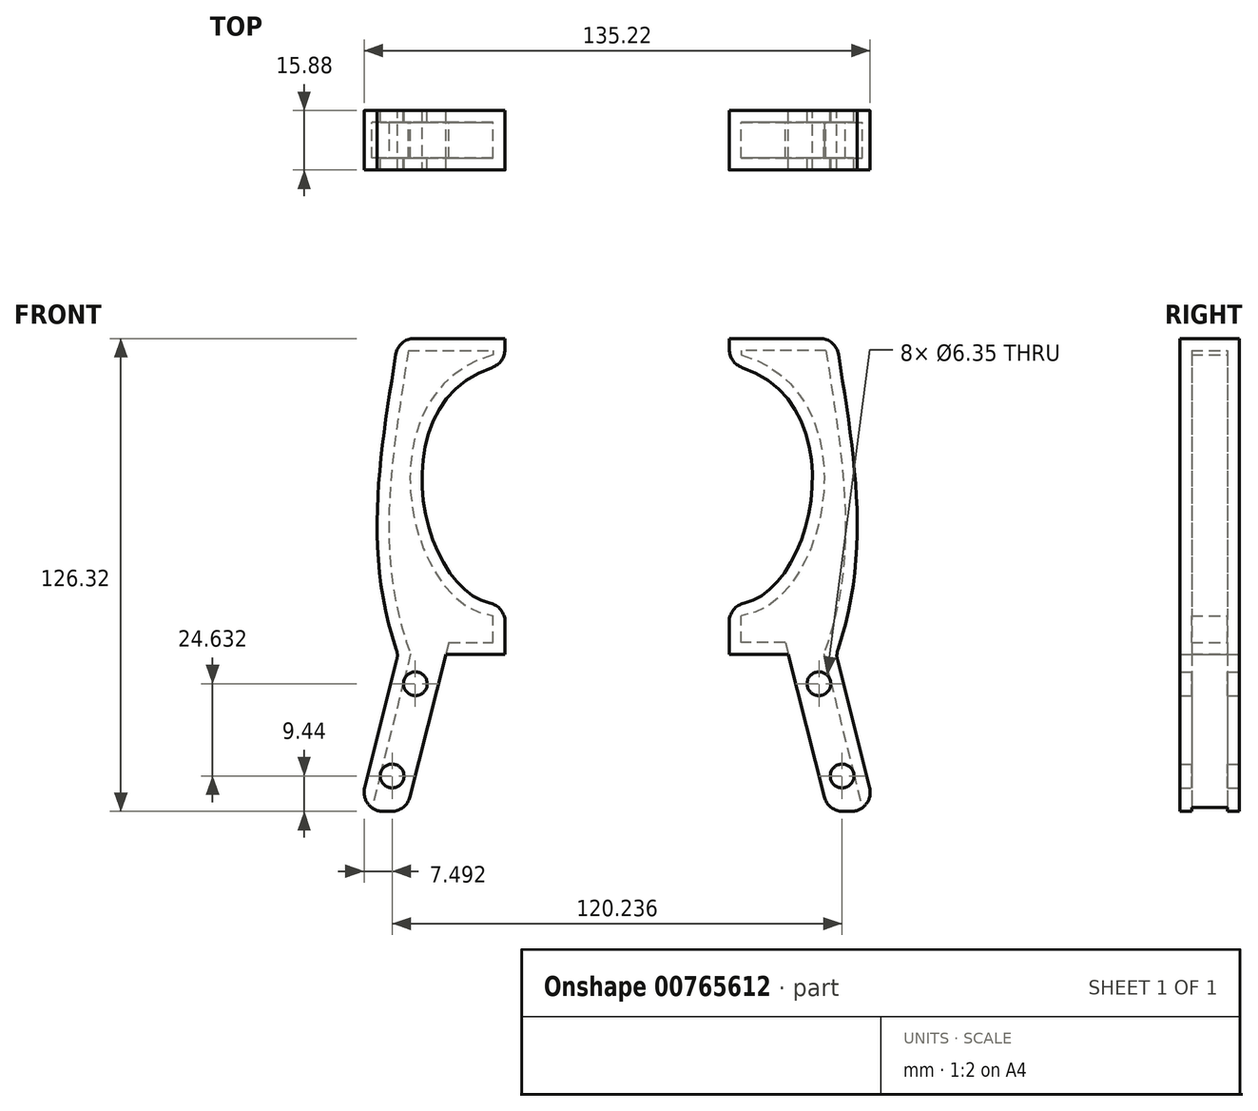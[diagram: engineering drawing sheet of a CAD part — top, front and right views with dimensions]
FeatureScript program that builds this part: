
annotation { "Feature Type Name" : "Feature", "Feature Type Description" : "" }
export const myFeature = defineFeature(function(context is Context, id is Id, definition is map)
    precondition{}
    {
        {
            var Q0;
            Q0=qCreatedBy(makeId("Front.planeOp"),FACE);
            var sketch = newSketch(context, id + "F0", { "sketchPlane" : qUnion([Q0])});
            skLineSegment(sketch, "E0", {"start": v(58.5, 0) * mm, "end": v(29.96, 0) * mm});
            skLineSegment(sketch, "E1.bottom", {"start": v(58.5, 0) * mm, "end": v(45.76, 0) * mm});
            skLineSegment(sketch, "E1.top", {"start": v(69.04, -41.87) * mm, "end": v(56.34, -41.87) * mm});
            skLineSegment(sketch, "E1.right", {"start": v(45.76, 0) * mm, "end": v(56.34, -41.87) * mm});
            skLineSegment(sketch, "E2", {"start": v(29.96, 0) * mm, "end": v(29.96, 13.6) * mm});
            skLineSegment(sketch, "E3", {"start": v(58.5, 84.45) * mm, "end": v(29.97, 84.45) * mm});
            skLineSegment(sketch, "E4", {"start": v(29.97, 84.45) * mm, "end": v(29.97, 77.65) * mm});
            skFitSpline(sketch, "E5", {"points": [v(29.97, 77.65) * mm, v(29.96, 13.6) * mm], "startDerivative": vector(109.54, -23.79) * mm, "endDerivative": vector(-65.23, 9.07) * mm});
            skLineSegment(sketch, "E6", {"start": v(58.5, 0) * mm, "end": v(69.04, -41.87) * mm});
            skFitSpline(sketch, "E7", {"points": [v(58.5, 84.45) * mm, v(58.5, 0) * mm], "startDerivative": vector(13, -87.28) * mm, "endDerivative": vector(-30.47, -85.42) * mm});
            skSolve(sketch);
        }
        {
            var Q0;
            Q0 = qSketchRegion(id + "F0", true);
            extrude(context, id + "F1", {"entities" : qUnion([Q0]), "depth" : 15.88 * mm, "offsetDistance" : 25.4 * mm});
        }
        {
            var Q0;
            Q0=makeQuery(id+"F1.opExtrude","SWEPT_FACE",FACE,{"disambiguationData":[OSD([sQuery(id+"F0.wireOp",EDGE,"E1.right")])]});
            var Q1;
            Q1=makeQuery(id+"F1.opExtrude","SWEPT_FACE",FACE,{"disambiguationData":[OSD([sQuery(id+"F0.wireOp",EDGE,"E1.top")])]});
            shell(context, id + "F2", {"entities" : qUnion([Q0, Q1]), "thickness" : 3.17 * mm});
        }
        {
            var Q0;
            Q0=makeQuery(id+"F1.opExtrude","CAP_FACE",FACE,{"disambiguationData":[OSD([sQuery(id+"F0.wireOp",EDGE,"DYzolfvh-CK0S-3XGK-zIts-vsUHT52ys9OM"),sQuery(id+"F0.wireOp",EDGE,"E0"),sQuery(id+"F0.wireOp",EDGE,"E1.top"),sQuery(id+"F0.wireOp",EDGE,"E1.left"),sQuery(id+"F0.wireOp",EDGE,"E1.right"),sQuery(id+"F0.wireOp",EDGE,"E2"),sQuery(id+"F0.wireOp",EDGE,"c781c78e-f2f3-4a78-be8b-957ab2571734"),sQuery(id+"F0.wireOp",EDGE,"wxyJcRo2-MiOi-M9DK-MjrB-uzMoI9jWQUQ4")])],"isStart":true});
            var sketch = newSketch(context, id + "F3", { "sketchPlane" : qUnion([Q0])});
            skCircle(sketch, "E8", {"center": v(-53.92, -7.8) * mm, "radius": 3.18 * mm});
            skCircle(sketch, "E9", {"center": v(-60.12, -32.43) * mm, "radius": 3.17 * mm});
            skSolve(sketch);
        }
        {
            var Q0;
            Q0 = qSketchRegion(id + "F3", true);
            extrude(context, id + "F4", {"entities" : qUnion([Q0]), "operationType" : NewBodyOperationType.REMOVE, "oppositeDirection" : true, "depth" : 25.4 * mm, "offsetDistance" : 25.4 * mm});
        }
        {
            var Q0;
            Q0=makeQuery(id+"F1.opExtrude","SWEPT_EDGE",EDGE,{"disambiguationData":[OSD([sQuery(id+"F0.wireOp",EDGE,"E4"),sQuery(id+"F0.wireOp",EDGE,"E5")])]});
            var Q1;
            Q1=makeQuery(id+"F1.opExtrude","SWEPT_EDGE",EDGE,{"disambiguationData":[OSD([sQuery(id+"F0.wireOp",EDGE,"E2"),sQuery(id+"F0.wireOp",EDGE,"E5")])]});
            var Q2;
            Q2=makeQuery(id+"F1.opExtrude","SWEPT_EDGE",EDGE,{"disambiguationData":[OSD([sQuery(id+"F0.wireOp",EDGE,"E1.top"),sQuery(id+"F0.wireOp",EDGE,"E1.left")])]});
            var Q3;
            Q3=makeQuery(id+"F2.opShell","OFFSET_EDGE",EDGE,{"disambiguationData":[OSD([sQuery(id+"F0.wireOp",EDGE,"E1.top"),sQuery(id+"F0.wireOp",EDGE,"E1.right")])]});
            var Q4;
            Q4=makeQuery(id+"F1.opExtrude","SWEPT_EDGE",EDGE,{"disambiguationData":[OSD([sQuery(id+"F0.wireOp",EDGE,"E1.bottom"),sQuery(id+"F0.wireOp",EDGE,"E6"),sQuery(id+"F0.wireOp",EDGE,"E7")])]});
            fillet(context, id + "F5", {"entities" : qUnion([Q0, Q1, Q2, Q3, Q4]), "radius" : 5.08 * mm, "tangentPropagation" : true, "allowEdgeOverflow" : false});
        }
        {
            var Q0;
            Q0=makeQuery(id+"F1.opExtrude","SWEPT_BODY",BODY,{"disambiguationData":[OSD([sQuery(id+"F0.wireOp",EDGE,"DYzolfvh-CK0S-3XGK-zIts-vsUHT52ys9OM"),sQuery(id+"F0.wireOp",EDGE,"E0"),sQuery(id+"F0.wireOp",EDGE,"E1.top"),sQuery(id+"F0.wireOp",EDGE,"E1.right"),sQuery(id+"F0.wireOp",EDGE,"E2"),sQuery(id+"F0.wireOp",EDGE,"NgdZD9qN-poD0-aQAS-fyzg-wJCO22ZVmQEB"),sQuery(id+"F0.wireOp",EDGE,"E3"),sQuery(id+"F0.wireOp",EDGE,"E4"),sQuery(id+"F0.wireOp",EDGE,"E5"),sQuery(id+"F0.wireOp",EDGE,"E6")])]});
            var Q1;
            Q1=qCreatedBy(makeId("Right.planeOp"),FACE);
            mirror(context, id + "F6", {"entities" : qUnion([Q0]), "mirrorPlane" : qUnion([Q1])});
        }
        {
            var Q0;
            Q0=makeQuery(id+"F1.opExtrude","SWEPT_EDGE",EDGE,{"disambiguationData":[OSD([sQuery(id+"F0.wireOp",EDGE,"E3"),sQuery(id+"F0.wireOp",EDGE,"E7")])]});
            var Q1;
            Q1=makeQuery(id+"F6.opPattern","COPY",EDGE,{"derivedFrom":makeQuery(id+"F1.opExtrude","SWEPT_EDGE",EDGE,{"disambiguationData":[OSD([sQuery(id+"F0.wireOp",EDGE,"E3"),sQuery(id+"F0.wireOp",EDGE,"E7")])]}),"instanceName":"1"});
            var Q2;
            Q2=makeQuery(id+"F2.opShell","OFFSET_EDGE",EDGE,{"disambiguationData":[OSD([sQuery(id+"F0.wireOp",EDGE,"E1.top"),sQuery(id+"F0.wireOp",EDGE,"E1.right")])]});
            fillet(context, id + "F7", {"entities" : qUnion([Q0, Q1, Q2]), "radius" : 5.08 * mm, "tangentPropagation" : true, "allowEdgeOverflow" : false});
        }
    });
